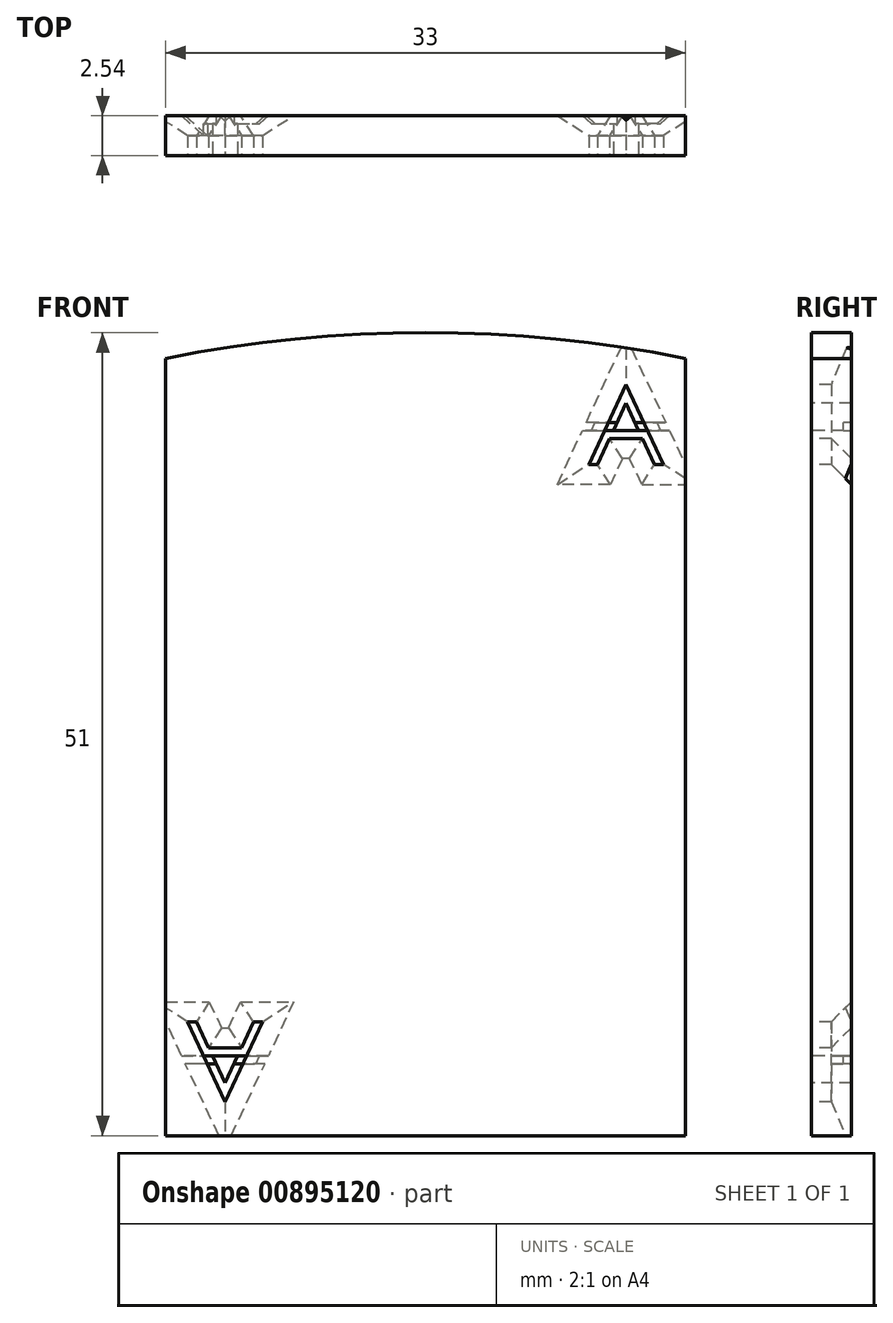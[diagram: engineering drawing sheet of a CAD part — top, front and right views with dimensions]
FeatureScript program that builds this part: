
annotation { "Feature Type Name" : "Feature", "Feature Type Description" : "" }
export const myFeature = defineFeature(function(context is Context, id is Id, definition is map)
    precondition{}
    {
        {
            var Q0;
            Q0=qCreatedBy(makeId("Front.planeOp"),FACE);
            var sketch = newSketch(context, id + "F0", { "sketchPlane" : qUnion([Q0])});
            skLineSegment(sketch, "E0", {"start": v(0, 49.37) * mm, "end": v(0, 0) * mm});
            skLineSegment(sketch, "E1", {"start": v(0, 0) * mm, "end": v(33, 0) * mm});
            skLineSegment(sketch, "E2", {"start": v(33, 0) * mm, "end": v(33, 49.37) * mm});
            skArc(sketch, "E3", {"start": v(33, 49.37) * mm, "mid": v(16.5, 51) * mm, "end": v(0, 49.37) * mm});
            skSolve(sketch);
        }
        {
            var Q0;
            Q0 = qSketchRegion(id + "F0", true);
            extrude(context, id + "F1", {"entities" : qUnion([Q0]), "depth" : 2.54 * mm, "offsetDistance" : 25.4 * mm});
        }
        {
            var Q0;
            Q0=makeQuery(id+"F1.opExtrude","CAP_FACE",FACE,{"disambiguationData":[OSD([sQuery(id+"F0.wireOp",EDGE,"E0"),sQuery(id+"F0.wireOp",EDGE,"E1"),sQuery(id+"F0.wireOp",EDGE,"E2"),sQuery(id+"F0.wireOp",EDGE,"E3")])],"isStart":false});
            var sketch = newSketch(context, id + "F2", { "sketchPlane" : qUnion([Q0])});
            skLineSegment(sketch, "E4", {"start": v(1.4, 42.64) * mm, "end": v(2.4, 44.8) * mm});
            skLineSegment(sketch, "E5", {"start": v(3.77, 47.72) * mm, "end": v(4.9, 45.31) * mm});
            skLineSegment(sketch, "E6", {"start": v(1.4, 42.64) * mm, "end": v(1.96, 42.64) * mm});
            skLineSegment(sketch, "E7", {"start": v(1.96, 42.64) * mm, "end": v(2.73, 44.3) * mm});
            skLineSegment(sketch, "E8", {"start": v(2.73, 44.3) * mm, "end": v(4.8, 44.3) * mm});
            skLineSegment(sketch, "E9", {"start": v(4.8, 44.3) * mm, "end": v(5.57, 42.64) * mm});
            skLineSegment(sketch, "E10", {"start": v(5.57, 42.64) * mm, "end": v(6.13, 42.64) * mm});
            skLineSegment(sketch, "E11", {"start": v(1.96, 42.64) * mm, "end": v(2.96, 44.8) * mm, "construction": true});
            skLineSegment(sketch, "E12", {"start": v(3.77, 46.52) * mm, "end": v(4.33, 45.31) * mm, "construction": true});
            skLineSegment(sketch, "E13", {"start": v(2.96, 44.8) * mm, "end": v(4.57, 44.8) * mm});
            skLineSegment(sketch, "E14", {"start": v(3.77, 44.8) * mm, "end": v(3.77, 47.72) * mm, "construction": true});
            skLineSegment(sketch, "E15", {"start": v(3.77, 44.8) * mm, "end": v(3.77, 42.64) * mm, "construction": true});
            skLineSegment(sketch, "E16", {"start": v(3.2, 45.31) * mm, "end": v(3.77, 46.52) * mm});
            skLineSegment(sketch, "E17", {"start": v(4.33, 45.31) * mm, "end": v(3.77, 46.52) * mm});
            skLineSegment(sketch, "E18", {"start": v(4.57, 44.8) * mm, "end": v(5.13, 44.8) * mm});
            skLineSegment(sketch, "E19", {"start": v(2.96, 44.8) * mm, "end": v(2.4, 44.8) * mm});
            skLineSegment(sketch, "E20", {"start": v(4.33, 45.31) * mm, "end": v(4.9, 45.31) * mm});
            skLineSegment(sketch, "E21", {"start": v(3.2, 45.31) * mm, "end": v(2.64, 45.31) * mm});
            skPoint(sketch, "E22", {"position": v(3.77, 45.31) * mm});
            skLineSegment(sketch, "E23.trimOffspring", {"start": v(2.64, 45.31) * mm, "end": v(3.77, 47.72) * mm});
            skLineSegment(sketch, "E24.trimOffspring", {"start": v(3.2, 45.31) * mm, "end": v(3.77, 46.52) * mm, "construction": true});
            skLineSegment(sketch, "E25.trimOffspring", {"start": v(4.57, 44.8) * mm, "end": v(5.57, 42.64) * mm, "construction": true});
            skLineSegment(sketch, "E26.trimOffspring", {"start": v(5.13, 44.8) * mm, "end": v(6.13, 42.64) * mm});
            skPoint(sketch, "E27.orphan", {"position": v(16.5, 51) * mm});
            skPoint(sketch, "E28.orphan", {"position": v(0, 24.69) * mm});
            skPoint(sketch, "E29.end.orphan", {"position": v(33, 24.69) * mm});
            skPoint(sketch, "E30.start.orphan", {"position": v(16.5, 0) * mm});
            skLineSegment(sketch, "E31", {"start": v(26.87, 7.24) * mm, "end": v(27.87, 5.08) * mm});
            skLineSegment(sketch, "E32", {"start": v(29.23, 2.16) * mm, "end": v(30.36, 4.57) * mm});
            skLineSegment(sketch, "E33", {"start": v(31.6, 7.24) * mm, "end": v(31.04, 7.24) * mm, "construction": true});
            skLineSegment(sketch, "E34", {"start": v(26.87, 7.24) * mm, "end": v(27.43, 7.24) * mm});
            skLineSegment(sketch, "E35", {"start": v(27.43, 7.24) * mm, "end": v(28.2, 5.59) * mm});
            skLineSegment(sketch, "E36", {"start": v(28.2, 5.59) * mm, "end": v(30.27, 5.59) * mm});
            skLineSegment(sketch, "E37", {"start": v(30.27, 5.59) * mm, "end": v(31.04, 7.24) * mm});
            skLineSegment(sketch, "E38", {"start": v(31.04, 7.24) * mm, "end": v(31.6, 7.24) * mm});
            skLineSegment(sketch, "E39.trimOffspring", {"start": v(27.43, 7.24) * mm, "end": v(26.87, 7.24) * mm, "construction": true});
            skLineSegment(sketch, "E40", {"start": v(27.87, 5.08) * mm, "end": v(30.6, 5.08) * mm});
            skLineSegment(sketch, "E41", {"start": v(28.67, 4.57) * mm, "end": v(29.23, 3.36) * mm});
            skLineSegment(sketch, "E42", {"start": v(29.23, 3.36) * mm, "end": v(29.8, 4.57) * mm});
            skLineSegment(sketch, "E43", {"start": v(28.1, 4.57) * mm, "end": v(28.67, 4.57) * mm});
            skLineSegment(sketch, "E44.trimOffspring", {"start": v(29.8, 4.57) * mm, "end": v(30.36, 4.57) * mm});
            skLineSegment(sketch, "E45.trimOffspring", {"start": v(28.1, 4.57) * mm, "end": v(29.23, 2.16) * mm});
            skLineSegment(sketch, "E46.trimOffspring", {"start": v(30.6, 5.08) * mm, "end": v(31.6, 7.24) * mm});
            skLineSegment(sketch, "E47", {"start": v(28.1, 4.57) * mm, "end": v(27.87, 5.08) * mm, "construction": true});
            skLineSegment(sketch, "E48", {"start": v(28.67, 4.57) * mm, "end": v(28.2, 5.59) * mm, "construction": true});
            skLineSegment(sketch, "E49", {"start": v(29.8, 4.57) * mm, "end": v(30.27, 5.59) * mm, "construction": true});
            skLineSegment(sketch, "E50", {"start": v(30.36, 4.57) * mm, "end": v(30.6, 5.08) * mm, "construction": true});
            skLineSegment(sketch, "E51", {"start": v(29.23, 2.16) * mm, "end": v(29.23, 7.24) * mm, "construction": true});
            skLineSegment(sketch, "E52", {"start": v(29.23, 7.24) * mm, "end": v(31.04, 7.24) * mm, "construction": true});
            skLineSegment(sketch, "E53", {"start": v(29.23, 7.24) * mm, "end": v(27.43, 7.24) * mm, "construction": true});
            skSolve(sketch);
        }
        {
            var Q0;
            Q0 = qSketchRegion(id + "F2", true);
            extrude(context, id + "F3", {"entities" : qUnion([Q0]), "operationType" : NewBodyOperationType.REMOVE, "oppositeDirection" : true, "depth" : 25.4 * mm, "offsetDistance" : 25.4 * mm});
        }
        {
            var Q0;
            Q0=makeQuery(id+"F1.opExtrude","CAP_FACE",FACE,{"disambiguationData":[OSD([sQuery(id+"F0.wireOp",EDGE,"E0"),sQuery(id+"F0.wireOp",EDGE,"E1"),sQuery(id+"F0.wireOp",EDGE,"E2"),sQuery(id+"F0.wireOp",EDGE,"E3")])],"isStart":false});
            var sketch = newSketch(context, id + "F4", { "sketchPlane" : qUnion([Q0])});
            skLineSegment(sketch, "E54", {"start": v(26.87, 7.24) * mm, "end": v(29.23, 2.16) * mm});
            skLineSegment(sketch, "E55", {"start": v(29.23, 2.16) * mm, "end": v(31.6, 7.24) * mm});
            skLineSegment(sketch, "E56", {"start": v(31.6, 7.24) * mm, "end": v(31.04, 7.24) * mm});
            skLineSegment(sketch, "E57", {"start": v(31.04, 7.24) * mm, "end": v(30.27, 5.59) * mm});
            skLineSegment(sketch, "E58", {"start": v(30.27, 5.59) * mm, "end": v(28.2, 5.59) * mm});
            skLineSegment(sketch, "E59", {"start": v(28.2, 5.59) * mm, "end": v(27.43, 7.24) * mm});
            skLineSegment(sketch, "E60", {"start": v(27.43, 7.24) * mm, "end": v(26.87, 7.24) * mm});
            skLineSegment(sketch, "E61", {"start": v(29.23, 3.36) * mm, "end": v(30.04, 5.08) * mm});
            skLineSegment(sketch, "E62", {"start": v(29.23, 3.36) * mm, "end": v(28.43, 5.08) * mm});
            skLineSegment(sketch, "E63", {"start": v(28.43, 5.08) * mm, "end": v(30.04, 5.08) * mm});
            skLineSegment(sketch, "E64", {"start": v(1.4, 42.64) * mm, "end": v(3.77, 47.72) * mm});
            skLineSegment(sketch, "E65", {"start": v(3.77, 47.72) * mm, "end": v(6.13, 42.64) * mm});
            skLineSegment(sketch, "E66", {"start": v(6.13, 42.64) * mm, "end": v(5.57, 42.64) * mm});
            skLineSegment(sketch, "E67", {"start": v(5.57, 42.64) * mm, "end": v(4.8, 44.3) * mm});
            skLineSegment(sketch, "E68", {"start": v(4.8, 44.3) * mm, "end": v(2.73, 44.3) * mm});
            skLineSegment(sketch, "E69", {"start": v(2.73, 44.3) * mm, "end": v(1.96, 42.64) * mm});
            skLineSegment(sketch, "E70", {"start": v(1.96, 42.64) * mm, "end": v(1.4, 42.64) * mm});
            skLineSegment(sketch, "E71", {"start": v(3.77, 46.52) * mm, "end": v(2.96, 44.8) * mm});
            skLineSegment(sketch, "E72", {"start": v(3.77, 46.52) * mm, "end": v(4.57, 44.8) * mm});
            skLineSegment(sketch, "E73", {"start": v(4.57, 44.8) * mm, "end": v(2.96, 44.8) * mm});
            skSolve(sketch);
        }
        {
            var Q0;
            Q0 = qSketchRegion(id + "F4", true);
            extrude(context, id + "F5", {"entities" : qUnion([Q0]), "operationType" : NewBodyOperationType.REMOVE, "oppositeDirection" : true, "depth" : 2.03 * mm, "offsetDistance" : 25.4 * mm});
        }
        {
            var Q0;
            Q0=makeQuery(id+"F3.boolean.opBoolean","INTERSECT",EDGE,{"derivedFrom":[makeQuery(id+"F1.opExtrude","CAP_FACE",FACE,{"disambiguationData":[OSD([sQuery(id+"F0.wireOp",EDGE,"E0"),sQuery(id+"F0.wireOp",EDGE,"E1"),sQuery(id+"F0.wireOp",EDGE,"E2"),sQuery(id+"F0.wireOp",EDGE,"E3")])],"isStart":true}),makeQuery(id+"F3.opExtrude","SWEPT_FACE",FACE,{"disambiguationData":[OSD([sQuery(id+"F2.wireOp",EDGE,"E38")])]})]});
            var Q1;
            Q1=makeQuery(id+"F3.boolean.opBoolean","INTERSECT",EDGE,{"derivedFrom":[makeQuery(id+"F1.opExtrude","CAP_FACE",FACE,{"disambiguationData":[OSD([sQuery(id+"F0.wireOp",EDGE,"E0"),sQuery(id+"F0.wireOp",EDGE,"E1"),sQuery(id+"F0.wireOp",EDGE,"E2"),sQuery(id+"F0.wireOp",EDGE,"E3")])],"isStart":true}),makeQuery(id+"F3.opExtrude","SWEPT_FACE",FACE,{"disambiguationData":[OSD([sQuery(id+"F2.wireOp",EDGE,"E37")])]})]});
            var Q2;
            Q2=makeQuery(id+"F3.boolean.opBoolean","INTERSECT",EDGE,{"derivedFrom":[makeQuery(id+"F1.opExtrude","CAP_FACE",FACE,{"disambiguationData":[OSD([sQuery(id+"F0.wireOp",EDGE,"E0"),sQuery(id+"F0.wireOp",EDGE,"E1"),sQuery(id+"F0.wireOp",EDGE,"E2"),sQuery(id+"F0.wireOp",EDGE,"E3")])],"isStart":true}),makeQuery(id+"F3.opExtrude","SWEPT_FACE",FACE,{"disambiguationData":[OSD([sQuery(id+"F2.wireOp",EDGE,"E36")])]})]});
            var Q3;
            Q3=makeQuery(id+"F3.boolean.opBoolean","INTERSECT",EDGE,{"derivedFrom":[makeQuery(id+"F1.opExtrude","CAP_FACE",FACE,{"disambiguationData":[OSD([sQuery(id+"F0.wireOp",EDGE,"E0"),sQuery(id+"F0.wireOp",EDGE,"E1"),sQuery(id+"F0.wireOp",EDGE,"E2"),sQuery(id+"F0.wireOp",EDGE,"E3")])],"isStart":true}),makeQuery(id+"F3.opExtrude","SWEPT_FACE",FACE,{"disambiguationData":[OSD([sQuery(id+"F2.wireOp",EDGE,"E35")])]})]});
            var Q4;
            Q4=makeQuery(id+"F3.boolean.opBoolean","INTERSECT",EDGE,{"derivedFrom":[makeQuery(id+"F1.opExtrude","CAP_FACE",FACE,{"disambiguationData":[OSD([sQuery(id+"F0.wireOp",EDGE,"E0"),sQuery(id+"F0.wireOp",EDGE,"E1"),sQuery(id+"F0.wireOp",EDGE,"E2"),sQuery(id+"F0.wireOp",EDGE,"E3")])],"isStart":true}),makeQuery(id+"F3.opExtrude","SWEPT_FACE",FACE,{"disambiguationData":[OSD([sQuery(id+"F2.wireOp",EDGE,"E34")])]})]});
            var Q5;
            Q5=makeQuery(id+"F3.boolean.opBoolean","INTERSECT",EDGE,{"derivedFrom":[makeQuery(id+"F1.opExtrude","CAP_FACE",FACE,{"disambiguationData":[OSD([sQuery(id+"F0.wireOp",EDGE,"E0"),sQuery(id+"F0.wireOp",EDGE,"E1"),sQuery(id+"F0.wireOp",EDGE,"E2"),sQuery(id+"F0.wireOp",EDGE,"E3")])],"isStart":true}),makeQuery(id+"F3.opExtrude","SWEPT_FACE",FACE,{"disambiguationData":[OSD([sQuery(id+"F2.wireOp",EDGE,"E31")])]})]});
            chamfer(context, id + "F6", {"entities" : qUnion([Q0, Q1, Q2, Q3, Q4, Q5]), "width" : 1.27 * mm, "tangentPropagation" : true});
        }
        {
            var Q0;
            Q0=makeQuery(id+"F3.boolean.opBoolean","INTERSECT",EDGE,{"derivedFrom":[makeQuery(id+"F1.opExtrude","CAP_FACE",FACE,{"disambiguationData":[OSD([sQuery(id+"F0.wireOp",EDGE,"E0"),sQuery(id+"F0.wireOp",EDGE,"E1"),sQuery(id+"F0.wireOp",EDGE,"E2"),sQuery(id+"F0.wireOp",EDGE,"E3")])],"isStart":true}),makeQuery(id+"F3.opExtrude","SWEPT_FACE",FACE,{"disambiguationData":[OSD([sQuery(id+"F2.wireOp",EDGE,"E46.trimOffspring")])]})]});
            var Q1;
            Q1=makeQuery(id+"F3.boolean.opBoolean","INTERSECT",EDGE,{"derivedFrom":[makeQuery(id+"F1.opExtrude","CAP_FACE",FACE,{"disambiguationData":[OSD([sQuery(id+"F0.wireOp",EDGE,"E0"),sQuery(id+"F0.wireOp",EDGE,"E1"),sQuery(id+"F0.wireOp",EDGE,"E2"),sQuery(id+"F0.wireOp",EDGE,"E3")])],"isStart":true}),makeQuery(id+"F3.opExtrude","SWEPT_FACE",FACE,{"disambiguationData":[OSD([sQuery(id+"F2.wireOp",EDGE,"E32")])]})]});
            chamfer(context, id + "F7", {"entities" : qUnion([Q0, Q1]), "width" : 1.27 * mm, "tangentPropagation" : true});
        }
        {
            var Q0;
            Q0=makeQuery(id+"F3.boolean.opBoolean","INTERSECT",EDGE,{"derivedFrom":[makeQuery(id+"F1.opExtrude","CAP_FACE",FACE,{"disambiguationData":[OSD([sQuery(id+"F0.wireOp",EDGE,"E0"),sQuery(id+"F0.wireOp",EDGE,"E1"),sQuery(id+"F0.wireOp",EDGE,"E2"),sQuery(id+"F0.wireOp",EDGE,"E3")])],"isStart":true}),makeQuery(id+"F3.opExtrude","SWEPT_FACE",FACE,{"disambiguationData":[OSD([sQuery(id+"F2.wireOp",EDGE,"E8")])]})]});
            var Q1;
            Q1=makeQuery(id+"F3.boolean.opBoolean","INTERSECT",EDGE,{"derivedFrom":[makeQuery(id+"F1.opExtrude","CAP_FACE",FACE,{"disambiguationData":[OSD([sQuery(id+"F0.wireOp",EDGE,"E0"),sQuery(id+"F0.wireOp",EDGE,"E1"),sQuery(id+"F0.wireOp",EDGE,"E2"),sQuery(id+"F0.wireOp",EDGE,"E3")])],"isStart":true}),makeQuery(id+"F3.opExtrude","SWEPT_FACE",FACE,{"disambiguationData":[OSD([sQuery(id+"F2.wireOp",EDGE,"E9")])]})]});
            var Q2;
            Q2=makeQuery(id+"F3.boolean.opBoolean","INTERSECT",EDGE,{"derivedFrom":[makeQuery(id+"F1.opExtrude","CAP_FACE",FACE,{"disambiguationData":[OSD([sQuery(id+"F0.wireOp",EDGE,"E0"),sQuery(id+"F0.wireOp",EDGE,"E1"),sQuery(id+"F0.wireOp",EDGE,"E2"),sQuery(id+"F0.wireOp",EDGE,"E3")])],"isStart":true}),makeQuery(id+"F3.opExtrude","SWEPT_FACE",FACE,{"disambiguationData":[OSD([sQuery(id+"F2.wireOp",EDGE,"E10")])]})]});
            var Q3;
            Q3=makeQuery(id+"F3.boolean.opBoolean","INTERSECT",EDGE,{"derivedFrom":[makeQuery(id+"F1.opExtrude","CAP_FACE",FACE,{"disambiguationData":[OSD([sQuery(id+"F0.wireOp",EDGE,"E0"),sQuery(id+"F0.wireOp",EDGE,"E1"),sQuery(id+"F0.wireOp",EDGE,"E2"),sQuery(id+"F0.wireOp",EDGE,"E3")])],"isStart":true}),makeQuery(id+"F3.opExtrude","SWEPT_FACE",FACE,{"disambiguationData":[OSD([sQuery(id+"F2.wireOp",EDGE,"E7")])]})]});
            var Q4;
            Q4=makeQuery(id+"F3.boolean.opBoolean","INTERSECT",EDGE,{"derivedFrom":[makeQuery(id+"F1.opExtrude","CAP_FACE",FACE,{"disambiguationData":[OSD([sQuery(id+"F0.wireOp",EDGE,"E0"),sQuery(id+"F0.wireOp",EDGE,"E1"),sQuery(id+"F0.wireOp",EDGE,"E2"),sQuery(id+"F0.wireOp",EDGE,"E3")])],"isStart":true}),makeQuery(id+"F3.opExtrude","SWEPT_FACE",FACE,{"disambiguationData":[OSD([sQuery(id+"F2.wireOp",EDGE,"E4")])]})]});
            var Q5;
            Q5=makeQuery(id+"F3.boolean.opBoolean","INTERSECT",EDGE,{"derivedFrom":[makeQuery(id+"F1.opExtrude","CAP_FACE",FACE,{"disambiguationData":[OSD([sQuery(id+"F0.wireOp",EDGE,"E0"),sQuery(id+"F0.wireOp",EDGE,"E1"),sQuery(id+"F0.wireOp",EDGE,"E2"),sQuery(id+"F0.wireOp",EDGE,"E3")])],"isStart":true}),makeQuery(id+"F3.opExtrude","SWEPT_FACE",FACE,{"disambiguationData":[OSD([sQuery(id+"F2.wireOp",EDGE,"E6")])]})]});
            chamfer(context, id + "F8", {"entities" : qUnion([Q0, Q1, Q2, Q3, Q4, Q5]), "width" : 1.27 * mm, "tangentPropagation" : true});
        }
        {
            var Q0;
            Q0=makeQuery(id+"F3.boolean.opBoolean","INTERSECT",EDGE,{"derivedFrom":[makeQuery(id+"F1.opExtrude","CAP_FACE",FACE,{"disambiguationData":[OSD([sQuery(id+"F0.wireOp",EDGE,"E0"),sQuery(id+"F0.wireOp",EDGE,"E1"),sQuery(id+"F0.wireOp",EDGE,"E2"),sQuery(id+"F0.wireOp",EDGE,"E3")])],"isStart":true}),makeQuery(id+"F3.opExtrude","SWEPT_FACE",FACE,{"disambiguationData":[OSD([sQuery(id+"F2.wireOp",EDGE,"E5")])]})]});
            chamfer(context, id + "F9", {"entities" : qUnion([Q0]), "width" : 1.27 * mm, "tangentPropagation" : true});
        }
        {
            var Q0;
            Q0=makeQuery(id+"F1.opExtrude","SWEPT_BODY",BODY,{"disambiguationData":[OSD([sQuery(id+"F0.wireOp",EDGE,"E0"),sQuery(id+"F0.wireOp",EDGE,"E1"),sQuery(id+"F0.wireOp",EDGE,"E2"),sQuery(id+"F0.wireOp",EDGE,"E3")])]});
            var Q1;
            Q1=qCreatedBy(makeId("Right.planeOp"),FACE);
            mirror(context, id + "F10", {"operationType" : NewBodyOperationType.ADD, "entities" : qUnion([Q0]), "mirrorPlane" : qUnion([Q1])});
        }
        {
            var Q0;
            {var subQ0=sQuery(id+"F0.wireOp",EDGE,"E2");var subQ1=sQuery(id+"F0.wireOp",EDGE,"E1");var subQ2=sQuery(id+"F0.wireOp",EDGE,"E3");var subQ3=sQuery(id+"F0.wireOp",EDGE,"E0");var subQ4=makeQuery(id+"F5.boolean.opBoolean","SPLIT",FACE,{"disambiguationData":[TD([makeQuery(id+"F1.opExtrude","SWEPT_FACE",FACE,{"disambiguationData":[OSD([subQ3])]})])],"derivedFrom":makeQuery(id+"F1.opExtrude","CAP_FACE",FACE,{"disambiguationData":[OSD([subQ3,subQ1,subQ0,subQ2])],"isStart":false})});Q0=makeQuery(id+"F10.boolean.opBoolean","MERGE",FACE,{"derivedFrom":[subQ4,makeQuery(id+"F10.opPattern","COPY",FACE,{"derivedFrom":subQ4,"instanceName":"1"})]});}
            var sketch = newSketch(context, id + "F11", { "sketchPlane" : qUnion([Q0])});
            skLineSegment(sketch, "E74", {"start": v(0, 49.37) * mm, "end": v(0, 0) * mm});
            skLineSegment(sketch, "E75", {"start": v(0, 0) * mm, "end": v(33, 0) * mm});
            skLineSegment(sketch, "E76", {"start": v(33, 0) * mm, "end": v(33, 49.37) * mm});
            skArc(sketch, "E77", {"start": v(33, 49.37) * mm, "mid": v(16.5, 51) * mm, "end": v(0, 49.37) * mm});
            skSolve(sketch);
        }
        {
            var Q0;
            Q0 = qSketchRegion(id + "F11", true);
            extrude(context, id + "F12", {"entities" : qUnion([Q0]), "operationType" : NewBodyOperationType.REMOVE, "endBound" : BoundingType.THROUGH_ALL, "oppositeDirection" : true, "depth" : 25.4 * mm, "offsetDistance" : 25.4 * mm});
        }
    });
